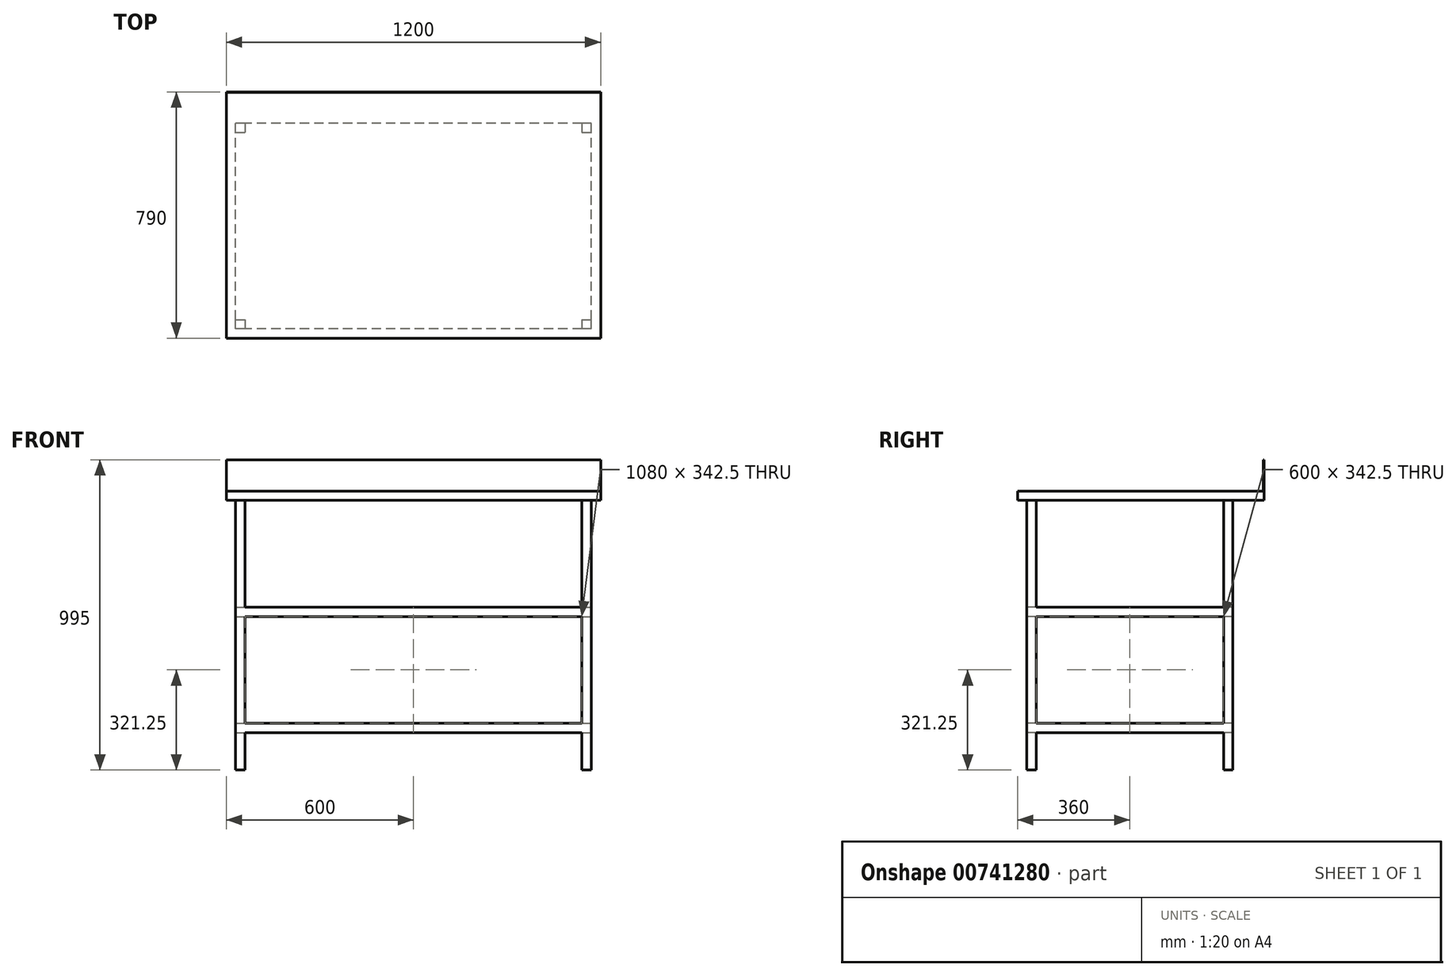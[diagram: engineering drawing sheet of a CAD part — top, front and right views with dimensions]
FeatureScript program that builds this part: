
annotation { "Feature Type Name" : "Feature", "Feature Type Description" : "" }
export const myFeature = defineFeature(function(context is Context, id is Id, definition is map)
    precondition{}
    {
        {
            var Q0;
            Q0=qCreatedBy(makeId("Right.planeOp"),FACE);
            var sketch = newSketch(context, id + "F0", { "sketchPlane" : qUnion([Q0])});
            skLineSegment(sketch, "E0", {"start": v(0, 0) * mm, "end": v(790, 0) * mm});
            skLineSegment(sketch, "E1", {"start": v(790, 0) * mm, "end": v(790, 130) * mm});
            skLineSegment(sketch, "E2", {"start": v(790, 130) * mm, "end": v(788, 130) * mm});
            skLineSegment(sketch, "E3", {"start": v(788, 130) * mm, "end": v(788, 30) * mm});
            skLineSegment(sketch, "E4", {"start": v(788, 30) * mm, "end": v(0, 30) * mm});
            skLineSegment(sketch, "E5", {"start": v(0, 30) * mm, "end": v(0, 0) * mm});
            skSolve(sketch);
        }
        {
            var Q0;
            Q0 = qSketchRegion(id + "F0", true);
            extrude(context, id + "F1", {"entities" : qUnion([Q0]), "depth" : 1200 * mm, "offsetDistance" : 25 * mm});
        }
        {
            var Q0;
            Q0=makeQuery(id+"F1.opExtrude","SWEPT_FACE",FACE,{"disambiguationData":[OSD([sQuery(id+"F0.wireOp",EDGE,"E0")])]});
            var sketch = newSketch(context, id + "F2", { "sketchPlane" : qUnion([Q0])});
            skLineSegment(sketch, "E6.bottom", {"start": v(60, -30) * mm, "end": v(30, -30) * mm});
            skLineSegment(sketch, "E6.top", {"start": v(60, -60) * mm, "end": v(30, -60) * mm});
            skLineSegment(sketch, "E6.left", {"start": v(60, -30) * mm, "end": v(60, -60) * mm});
            skLineSegment(sketch, "E6.right", {"start": v(30, -30) * mm, "end": v(30, -60) * mm});
            skPoint(sketch, "E6.middle", {"position": v(45, -45) * mm});
            skLineSegment(sketch, "E7.bottom", {"start": v(1170, -30) * mm, "end": v(1140, -30) * mm});
            skLineSegment(sketch, "E7.top", {"start": v(1170, -60) * mm, "end": v(1140, -60) * mm});
            skLineSegment(sketch, "E7.left", {"start": v(1170, -30) * mm, "end": v(1170, -60) * mm});
            skLineSegment(sketch, "E7.right", {"start": v(1140, -30) * mm, "end": v(1140, -60) * mm});
            skPoint(sketch, "E7.middle", {"position": v(1155, -45) * mm});
            skLineSegment(sketch, "E8.bottom", {"start": v(1170, -660) * mm, "end": v(1140, -660) * mm});
            skLineSegment(sketch, "E8.top", {"start": v(1170, -690) * mm, "end": v(1140, -690) * mm});
            skLineSegment(sketch, "E8.left", {"start": v(1170, -660) * mm, "end": v(1170, -690) * mm});
            skLineSegment(sketch, "E8.right", {"start": v(1140, -660) * mm, "end": v(1140, -690) * mm});
            skPoint(sketch, "E8.middle", {"position": v(1155, -675) * mm});
            skPoint(sketch, "E8.middle.positionSnap0", {"position": v(1155, -60) * mm});
            skPoint(sketch, "E8.centerSnap0", {"position": v(1155, -60) * mm});
            skLineSegment(sketch, "E9.bottom", {"start": v(60, -660) * mm, "end": v(30, -660) * mm});
            skLineSegment(sketch, "E9.top", {"start": v(60, -690) * mm, "end": v(30, -690) * mm});
            skLineSegment(sketch, "E9.left", {"start": v(60, -660) * mm, "end": v(60, -690) * mm});
            skLineSegment(sketch, "E9.right", {"start": v(30, -660) * mm, "end": v(30, -690) * mm});
            skPoint(sketch, "E9.middle", {"position": v(45, -675) * mm});
            skPoint(sketch, "E9.middle.positionSnap0", {"position": v(45, -60) * mm});
            skPoint(sketch, "E9.centerSnap0", {"position": v(45, -60) * mm});
            skSolve(sketch);
        }
        {
            var Q0;
            Q0 = qSketchRegion(id + "F2", true);
            extrude(context, id + "F3", {"entities" : qUnion([Q0]), "operationType" : NewBodyOperationType.ADD, "depth" : 865 * mm, "offsetDistance" : 25 * mm});
        }
        {
            var Q0;
            Q0=makeQuery(id+"F3.opExtrude","SWEPT_FACE",FACE,{"disambiguationData":[OSD([sQuery(id+"F2.wireOp",EDGE,"E6.left")])]});
            cPlane(context, id + "F4", {"entities" : qUnion([Q0]), "cplaneType" : CPlaneType.OFFSET, "offset" : 25 * mm, "width" : 150 * mm, "height" : 150 * mm});
        }
        {
            var Q0;
            Q0=qCreatedBy(id+"F4.planeOp",FACE);
            var sketch = newSketch(context, id + "F5", { "sketchPlane" : qUnion([Q0])});
            skLineSegment(sketch, "E10.bottom", {"start": v(30, -715) * mm, "end": v(690, -715) * mm});
            skLineSegment(sketch, "E10.top", {"start": v(30, -745) * mm, "end": v(690, -745) * mm});
            skLineSegment(sketch, "E10.left", {"start": v(30, -715) * mm, "end": v(30, -745) * mm});
            skLineSegment(sketch, "E10.right", {"start": v(690, -715) * mm, "end": v(690, -745) * mm});
            skSolve(sketch);
        }
        {
            var Q0;
            Q0 = qSketchRegion(id + "F5", true);
            var Q1;
            Q1=makeQuery(id+"F3.opExtrude","SWEPT_FACE",FACE,{"disambiguationData":[OSD([sQuery(id+"F2.wireOp",EDGE,"E7.left")])]});
            var Q2;
            Q2=makeQuery(id+"F3.opExtrude","SWEPT_FACE",FACE,{"disambiguationData":[OSD([sQuery(id+"F2.wireOp",EDGE,"E6.right")])]});
            extrude(context, id + "F6", {"entities" : qUnion([Q0]), "operationType" : NewBodyOperationType.ADD, "endBound" : BoundingType.UP_TO_SURFACE, "depth" : 25 * mm, "endBoundEntityFace" : qUnion([Q1]), "offsetDistance" : 25 * mm, "hasSecondDirection" : true, "secondDirectionBound" : SecondDirectionBoundingType.UP_TO_SURFACE, "secondDirectionOppositeDirection" : true, "secondDirectionDepth" : 25 * mm, "secondDirectionBoundEntityFace" : qUnion([Q2])});
        }
        {
            var Q0;
            Q0=qCreatedBy(id+"F4.planeOp",FACE);
            var sketch = newSketch(context, id + "F7", { "sketchPlane" : qUnion([Q0])});
            skLineSegment(sketch, "E11.bottom", {"start": v(30, -342.5) * mm, "end": v(690, -342.5) * mm});
            skLineSegment(sketch, "E11.top", {"start": v(30, -372.5) * mm, "end": v(690, -372.5) * mm});
            skLineSegment(sketch, "E11.left", {"start": v(30, -342.5) * mm, "end": v(30, -372.5) * mm});
            skLineSegment(sketch, "E11.right", {"start": v(690, -342.5) * mm, "end": v(690, -372.5) * mm});
            skSolve(sketch);
        }
        {
            var Q0;
            Q0 = qSketchRegion(id + "F7", true);
            var Q1;
            {var subQ0=sQuery(id+"F2.wireOp",EDGE,"E7.left");Q1=makeQuery(id+"F6.boolean.opBoolean","MERGE",FACE,{"derivedFrom":[makeQuery(id+"F3.opExtrude","SWEPT_FACE",FACE,{"disambiguationData":[OSD([subQ0])]}),makeQuery(id+"F3.opExtrude","SWEPT_FACE",FACE,{"disambiguationData":[OSD([sQuery(id+"F2.wireOp",EDGE,"E8.left")])]}),makeQuery(id+"F6.opExtrude","CAP_FACE",FACE,{"disambiguationData":[OSD([subQ0])],"isStart":false})]});}
            var Q2;
            {var subQ0=sQuery(id+"F2.wireOp",EDGE,"E6.right");Q2=makeQuery(id+"F6.boolean.opBoolean","MERGE",FACE,{"derivedFrom":[makeQuery(id+"F3.opExtrude","SWEPT_FACE",FACE,{"disambiguationData":[OSD([subQ0])]}),makeQuery(id+"F3.opExtrude","SWEPT_FACE",FACE,{"disambiguationData":[OSD([sQuery(id+"F2.wireOp",EDGE,"E9.right")])]}),makeQuery(id+"F6.opExtrude","CAP_FACE",FACE,{"disambiguationData":[OSD([subQ0])],"isStart":true})]});}
            extrude(context, id + "F8", {"entities" : qUnion([Q0]), "operationType" : NewBodyOperationType.ADD, "endBound" : BoundingType.UP_TO_SURFACE, "depth" : 25 * mm, "endBoundEntityFace" : qUnion([Q1]), "offsetDistance" : 25 * mm, "hasSecondDirection" : true, "secondDirectionBound" : SecondDirectionBoundingType.UP_TO_SURFACE, "secondDirectionOppositeDirection" : true, "secondDirectionDepth" : 25 * mm, "secondDirectionBoundEntityFace" : qUnion([Q2])});
        }
    });
